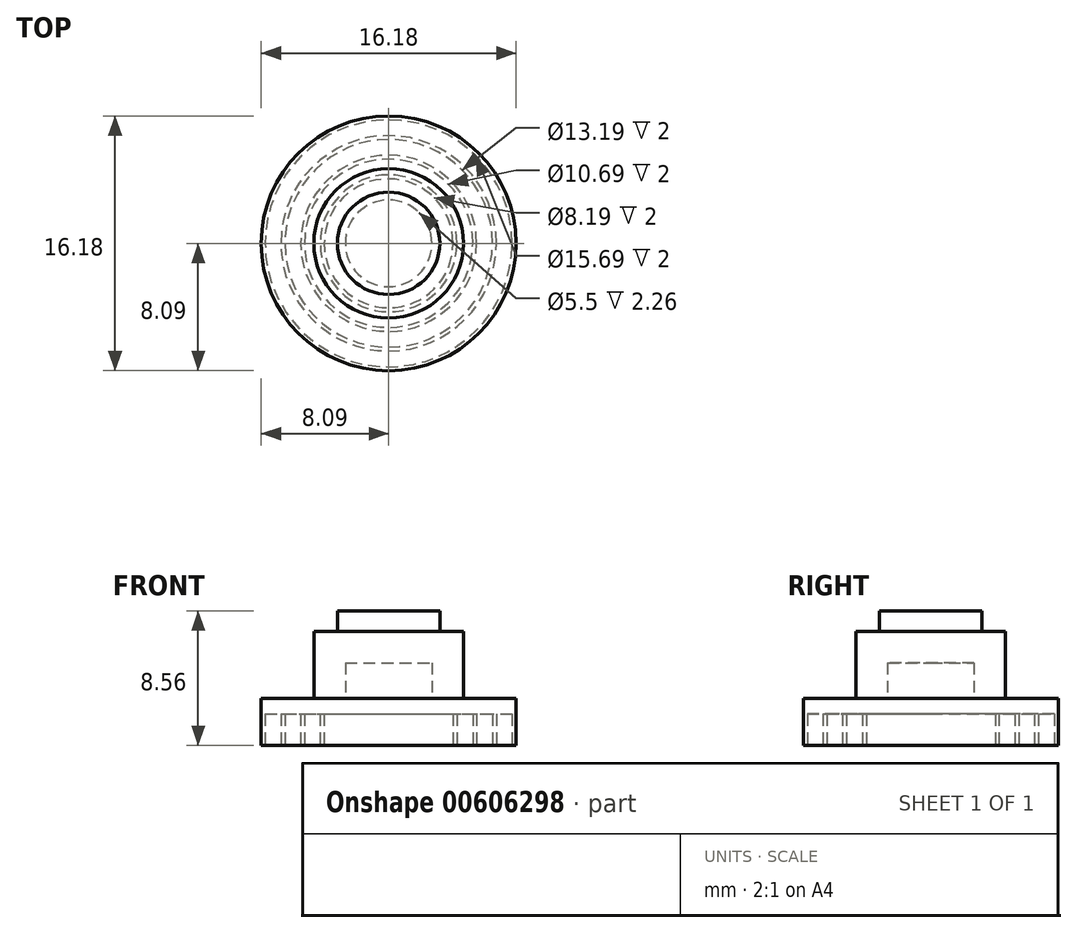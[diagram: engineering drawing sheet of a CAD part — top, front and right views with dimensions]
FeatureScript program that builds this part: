
annotation { "Feature Type Name" : "Feature", "Feature Type Description" : "" }
export const myFeature = defineFeature(function(context is Context, id is Id, definition is map)
    precondition{}
    {
        {
            var Q0;
            Q0=qCreatedBy(makeId("Front.planeOp"),FACE);
            var sketch = newSketch(context, id + "F0", { "sketchPlane" : qUnion([Q0])});
            skLineSegment(sketch, "E0", {"start": v(0, 5.56) * mm, "end": v(-3.25, 5.56) * mm});
            skLineSegment(sketch, "E1", {"start": v(-3.25, 5.56) * mm, "end": v(-3.25, 4.26) * mm});
            skLineSegment(sketch, "E2", {"start": v(-4.75, 0) * mm, "end": v(-2.75, 0) * mm});
            skLineSegment(sketch, "E3", {"start": v(-3.25, 4.26) * mm, "end": v(-4.75, 4.26) * mm});
            skLineSegment(sketch, "E4", {"start": v(-4.75, 4.26) * mm, "end": v(-4.75, 0) * mm});
            skLineSegment(sketch, "E5", {"start": v(-2.75, 0) * mm, "end": v(-2.75, 2.26) * mm});
            skLineSegment(sketch, "E6", {"start": v(-2.75, 2.26) * mm, "end": v(0, 2.26) * mm});
            skLineSegment(sketch, "E7", {"start": v(0, 2.26) * mm, "end": v(0, 5.56) * mm});
            skLineSegment(sketch, "E8.2", {"start": v(-6.23, 0) * mm, "end": v(-2.55, 0) * mm});
            skLineSegment(sketch, "E9", {"start": v(-6.23, 0) * mm, "end": v(-8.1, 0) * mm});
            skLineSegment(sketch, "E10", {"start": v(-8.1, 0) * mm, "end": v(-8.1, -3) * mm});
            skLineSegment(sketch, "E11", {"start": v(-8.1, -3) * mm, "end": v(-7.84, -3) * mm});
            skLineSegment(sketch, "E12", {"start": v(-7.84, -3) * mm, "end": v(-7.84, -1) * mm});
            skLineSegment(sketch, "E13", {"start": v(-7.84, -1) * mm, "end": v(0, -1) * mm});
            skLineSegment(sketch, "E14", {"start": v(0, -1) * mm, "end": v(0, 2.26) * mm});
            skLineSegment(sketch, "E15", {"start": v(-6.84, -1) * mm, "end": v(-6.84, -3) * mm});
            skLineSegment(sketch, "E16", {"start": v(-6.84, -3) * mm, "end": v(-6.6, -3) * mm});
            skLineSegment(sketch, "E17", {"start": v(-6.6, -3) * mm, "end": v(-6.6, -1) * mm});
            skLineSegment(sketch, "E18.1.0.0", {"start": v(-5.6, -1) * mm, "end": v(-5.6, -3) * mm});
            skLineSegment(sketch, "E18.1.0.1", {"start": v(-5.34, -3) * mm, "end": v(-5.34, -1) * mm});
            skLineSegment(sketch, "E18.1.0.2", {"start": v(-5.6, -3) * mm, "end": v(-5.34, -3) * mm});
            skLineSegment(sketch, "E18.2.0.0", {"start": v(-4.34, -1) * mm, "end": v(-4.34, -3) * mm});
            skLineSegment(sketch, "E18.2.0.1", {"start": v(-4.1, -3) * mm, "end": v(-4.1, -1) * mm});
            skLineSegment(sketch, "E18.2.0.2", {"start": v(-4.34, -3) * mm, "end": v(-4.1, -3) * mm});
            skLineSegment(sketch, "E18.direction1", {"start": v(-6.84, -3) * mm, "end": v(-5.6, -3) * mm, "construction": true});
            skLineSegment(sketch, "E19.0.3.0", {"start": v(-3.1, -1) * mm, "end": v(-3.1, -3) * mm});
            skLineSegment(sketch, "E19.3.3.0", {"start": v(-2.84, -3) * mm, "end": v(-2.84, -1) * mm});
            skLineSegment(sketch, "E19.6.3.0", {"start": v(-3.1, -3) * mm, "end": v(-2.84, -3) * mm});
            skLineSegment(sketch, "E20.0.4.0", {"start": v(-1.84, -1) * mm, "end": v(-1.84, -3) * mm});
            skLineSegment(sketch, "E20.3.4.0", {"start": v(-1.6, -3) * mm, "end": v(-1.6, -1) * mm});
            skLineSegment(sketch, "E20.6.4.0", {"start": v(-1.84, -3) * mm, "end": v(-1.6, -3) * mm});
            skSolve(sketch);
        }
        {
            var Q0;
            Q0=makeQuery(id+"F0.imprint","IMPRINT",FACE,{"disambiguationData":[TD([[makeQuery(id+"F0.imprint","IMPRINT",EDGE,{"derivedFrom":sQuery(id+"F0.wireOp",EDGE,"E0")}),1.0]])]});
            var Q1;
            Q1=sQuery(id+"F0.wireOp",EDGE,"E7");
            revolve(context, id + "F1", {"entities" : qUnion([Q0]), "axis" : qUnion([Q1]), "revolveType" : RevolveType.FULL});
        }
        {
            var Q0;
            Q0=makeQuery(id+"F0.imprint","IMPRINT",FACE,{"disambiguationData":[TD([[makeQuery(id+"F0.imprint","IMPRINT",EDGE,{"derivedFrom":sQuery(id+"F0.wireOp",EDGE,"E8.0")}),-1.0]])]});
            var Q1;
            {var subQ0=sQuery(id+"F0.wireOp",EDGE,"E15");Q1=makeQuery(id+"F0.imprint","IMPRINT",FACE,{"disambiguationData":[TD([[makeQuery(id+"F0.imprint","IMPRINT",EDGE,{"derivedFrom":subQ0}),1.0]])]});}
            var Q2;
            {var subQ0=sQuery(id+"F0.wireOp",EDGE,"E18.1.0.0");Q2=makeQuery(id+"F0.imprint","IMPRINT",FACE,{"disambiguationData":[TD([[makeQuery(id+"F0.imprint","IMPRINT",EDGE,{"derivedFrom":subQ0}),1.0]])]});}
            var Q3;
            {var subQ0=sQuery(id+"F0.wireOp",EDGE,"E18.2.0.0");Q3=makeQuery(id+"F0.imprint","IMPRINT",FACE,{"disambiguationData":[TD([[makeQuery(id+"F0.imprint","IMPRINT",EDGE,{"derivedFrom":subQ0}),1.0]])]});}
            var Q4;
            {var subQ0=sQuery(id+"F0.wireOp",EDGE,"E18.3.0.0");Q4=makeQuery(id+"F0.imprint","IMPRINT",FACE,{"disambiguationData":[TD([[makeQuery(id+"F0.imprint","IMPRINT",EDGE,{"derivedFrom":subQ0}),1.0]])]});}
            var Q5;
            {var subQ0=sQuery(id+"F0.wireOp",EDGE,"E18.4.0.0");Q5=makeQuery(id+"F0.imprint","IMPRINT",FACE,{"disambiguationData":[TD([[makeQuery(id+"F0.imprint","IMPRINT",EDGE,{"derivedFrom":subQ0}),1.0]])]});}
            var Q6;
            {var subQ0=sQuery(id+"F0.wireOp",EDGE,"E18.5.0.0");Q6=makeQuery(id+"F0.imprint","IMPRINT",FACE,{"disambiguationData":[TD([[makeQuery(id+"F0.imprint","IMPRINT",EDGE,{"derivedFrom":subQ0}),1.0]])]});}
            var Q7;
            {var subQ0=sQuery(id+"F0.wireOp",EDGE,"E18.6.0.0");Q7=makeQuery(id+"F0.imprint","IMPRINT",FACE,{"disambiguationData":[TD([[makeQuery(id+"F0.imprint","IMPRINT",EDGE,{"derivedFrom":subQ0}),1.0]])]});}
            var Q8;
            {var subQ2=sQuery(id+"F0.wireOp",EDGE,"E18.6.0.1");Q8=makeQuery(id+"F0.imprint","IMPRINT",FACE,{"disambiguationData":[TD([[makeQuery(id+"F0.imprint","IMPRINT",EDGE,{"derivedFrom":subQ2}),-1.0]])]});}
            var Q9;
            {var subQ16=sQuery(id+"F0.wireOp",EDGE,"E5");Q9=makeQuery(id+"F0.imprint","IMPRINT",FACE,{"disambiguationData":[TD([[makeQuery(id+"F0.imprint","IMPRINT",EDGE,{"derivedFrom":subQ16}),-1.0]])]});}
            var Q10;
            Q10=sQuery(id+"F0.wireOp",EDGE,"E14");
            revolve(context, id + "F2", {"entities" : qUnion([Q0, Q1, Q2, Q3, Q4, Q5, Q6, Q7, Q8, Q9]), "axis" : qUnion([Q10]), "revolveType" : RevolveType.FULL});
        }
    });
